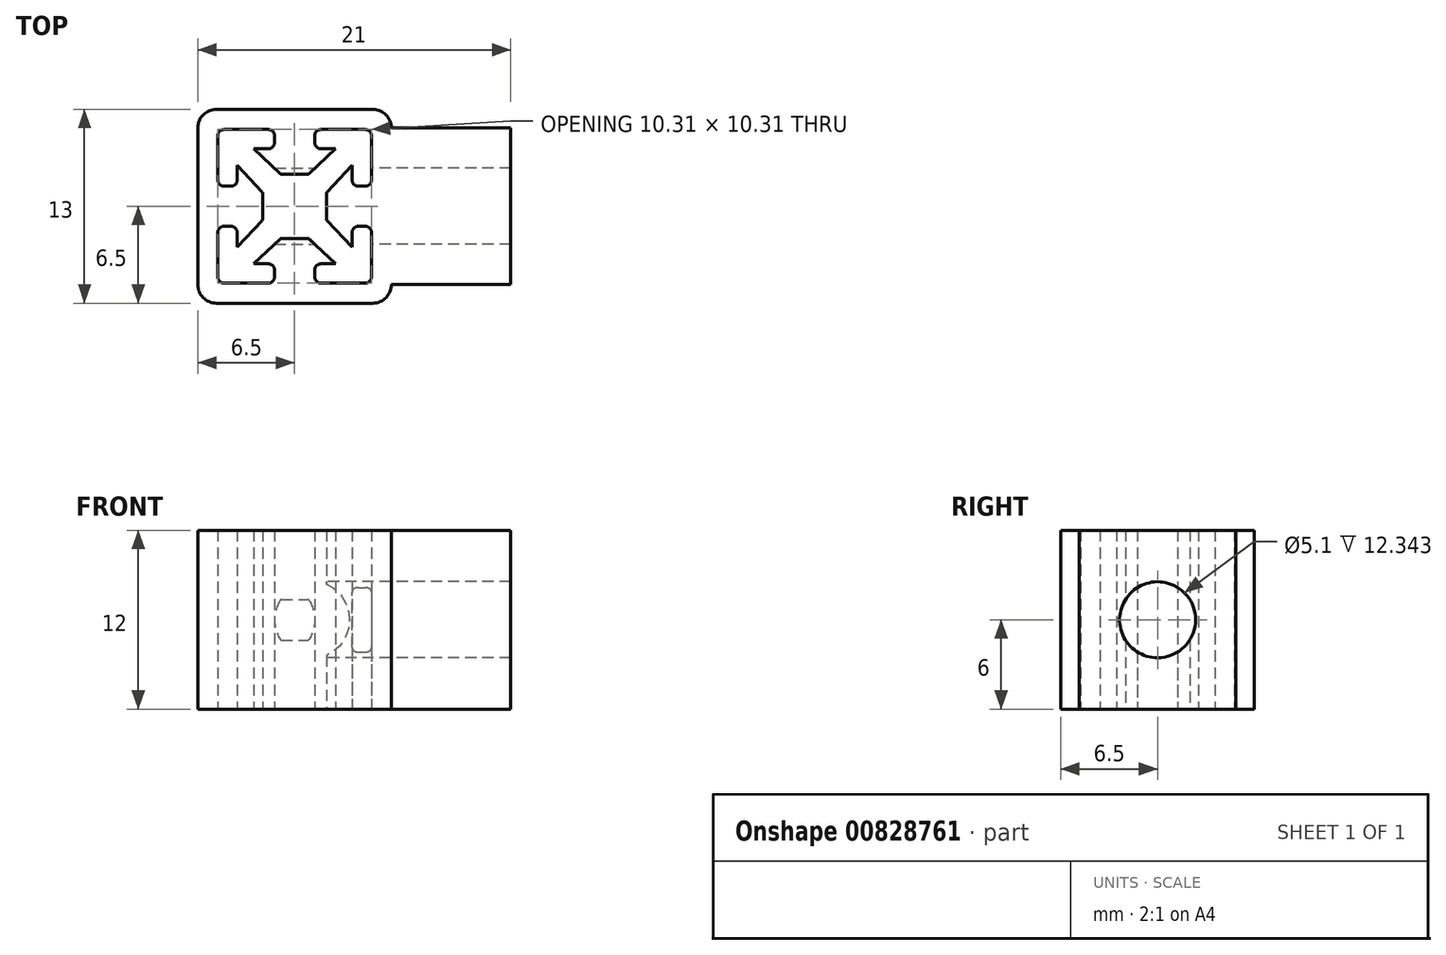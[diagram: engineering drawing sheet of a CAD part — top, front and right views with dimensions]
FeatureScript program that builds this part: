
annotation { "Feature Type Name" : "Feature", "Feature Type Description" : "" }
export const myFeature = defineFeature(function(context is Context, id is Id, definition is map)
    precondition{}
    {
        {
            var Q0;
            Q0=qCreatedBy(makeId("Top.planeOp"),FACE);
            var sketch = newSketch(context, id + "F0", { "sketchPlane" : qUnion([Q0])});
            skArc(sketch, "E0.0", {"start": v(6.5, 5.25) * mm, "mid": v(6.13, 6.13) * mm, "end": v(5.25, 6.5) * mm});
            skLineSegment(sketch, "E0.1", {"start": v(6.5, -5.25) * mm, "end": v(6.5, 5.25) * mm});
            skLineSegment(sketch, "E0.2", {"start": v(5.25, 6.5) * mm, "end": v(-5.25, 6.5) * mm});
            skArc(sketch, "E0.3", {"start": v(5.25, -6.5) * mm, "mid": v(6.13, -6.13) * mm, "end": v(6.5, -5.25) * mm});
            skArc(sketch, "E0.4", {"start": v(-5.25, 6.5) * mm, "mid": v(-6.13, 6.13) * mm, "end": v(-6.5, 5.25) * mm});
            skLineSegment(sketch, "E0.5", {"start": v(-6.5, 5.25) * mm, "end": v(-6.5, -5.25) * mm});
            skArc(sketch, "E0.6", {"start": v(-6.5, -5.25) * mm, "mid": v(-6.13, -6.13) * mm, "end": v(-5.25, -6.5) * mm});
            skLineSegment(sketch, "E0.7", {"start": v(-5.25, -6.5) * mm, "end": v(5.25, -6.5) * mm});
            skSolve(sketch);
        }
        {
            var Q0;
            Q0=qSketchRegion(id+"F0",true);
            extrude(context, id + "F1", {"entities" : qUnion([Q0]), "endBound" : BoundingType.SYMMETRIC, "oppositeDirection" : true, "depth" : 12 * mm, "offsetDistance" : 25 * mm});
        }
        {
            var Q0;
            Q0=qCreatedBy(makeId("Top.planeOp"),FACE);
            var sketch = newSketch(context, id + "F2", { "sketchPlane" : qUnion([Q0])});
            skLineSegment(sketch, "E1.0", {"start": v(0.96, -2.18) * mm, "end": v(2.75, -3.86) * mm});
            skArc(sketch, "E1.1", {"start": v(0.96, -2.18) * mm, "mid": v(0.93, -2.16) * mm, "end": v(0.89, -2.16) * mm});
            skLineSegment(sketch, "E1.2", {"start": v(0.89, -2.16) * mm, "end": v(-0.89, -2.16) * mm});
            skArc(sketch, "E1.3", {"start": v(-0.89, -2.16) * mm, "mid": v(-0.93, -2.16) * mm, "end": v(-0.96, -2.18) * mm});
            skLineSegment(sketch, "E1.4", {"start": v(-0.96, -2.18) * mm, "end": v(-2.75, -3.86) * mm});
            skLineSegment(sketch, "E1.5", {"start": v(-2.75, -3.86) * mm, "end": v(-1.75, -3.86) * mm});
            skArc(sketch, "E1.6", {"start": v(-1.35, -4.27) * mm, "mid": v(-1.47, -3.98) * mm, "end": v(-1.75, -3.86) * mm});
            skLineSegment(sketch, "E1.7", {"start": v(-1.35, -4.27) * mm, "end": v(-1.35, -4.75) * mm});
            skArc(sketch, "E1.8", {"start": v(-1.75, -5.15) * mm, "mid": v(-1.47, -5.04) * mm, "end": v(-1.35, -4.75) * mm});
            skLineSegment(sketch, "E1.9", {"start": v(-1.75, -5.15) * mm, "end": v(-4.75, -5.15) * mm});
            skArc(sketch, "E1.10", {"start": v(-5.15, -4.75) * mm, "mid": v(-5.04, -5.04) * mm, "end": v(-4.75, -5.15) * mm});
            skLineSegment(sketch, "E1.11", {"start": v(-5.15, -1.75) * mm, "end": v(-5.15, -4.75) * mm});
            skArc(sketch, "E1.12", {"start": v(-4.75, -1.35) * mm, "mid": v(-5.04, -1.47) * mm, "end": v(-5.15, -1.75) * mm});
            skLineSegment(sketch, "E1.13", {"start": v(-4.27, -1.35) * mm, "end": v(-4.75, -1.35) * mm});
            skArc(sketch, "E1.14", {"start": v(-3.86, -1.75) * mm, "mid": v(-3.98, -1.47) * mm, "end": v(-4.27, -1.35) * mm});
            skLineSegment(sketch, "E1.15", {"start": v(-3.86, -2.75) * mm, "end": v(-3.86, -1.75) * mm});
            skLineSegment(sketch, "E1.16", {"start": v(-2.18, -0.96) * mm, "end": v(-3.86, -2.75) * mm});
            skArc(sketch, "E1.17", {"start": v(-2.18, -0.96) * mm, "mid": v(-2.16, -0.93) * mm, "end": v(-2.16, -0.89) * mm});
            skArc(sketch, "E1.18", {"start": v(5.15, 4.75) * mm, "mid": v(5.04, 5.04) * mm, "end": v(4.75, 5.15) * mm});
            skLineSegment(sketch, "E1.19", {"start": v(5.15, 1.75) * mm, "end": v(5.15, 4.75) * mm});
            skArc(sketch, "E1.20", {"start": v(4.75, 1.35) * mm, "mid": v(5.04, 1.47) * mm, "end": v(5.15, 1.75) * mm});
            skLineSegment(sketch, "E1.21", {"start": v(4.27, 1.35) * mm, "end": v(4.75, 1.35) * mm});
            skArc(sketch, "E1.22", {"start": v(3.86, 1.75) * mm, "mid": v(3.98, 1.47) * mm, "end": v(4.27, 1.35) * mm});
            skLineSegment(sketch, "E1.23", {"start": v(3.86, 2.75) * mm, "end": v(3.86, 1.75) * mm});
            skLineSegment(sketch, "E1.24", {"start": v(2.18, 0.96) * mm, "end": v(3.86, 2.75) * mm});
            skArc(sketch, "E1.25", {"start": v(2.18, 0.96) * mm, "mid": v(2.16, 0.93) * mm, "end": v(2.16, 0.89) * mm});
            skLineSegment(sketch, "E1.26", {"start": v(2.16, 0.89) * mm, "end": v(2.16, -0.89) * mm});
            skArc(sketch, "E1.27", {"start": v(2.16, -0.89) * mm, "mid": v(2.16, -0.93) * mm, "end": v(2.18, -0.96) * mm});
            skLineSegment(sketch, "E1.28", {"start": v(2.18, -0.96) * mm, "end": v(3.86, -2.75) * mm});
            skLineSegment(sketch, "E1.29", {"start": v(3.86, -2.75) * mm, "end": v(3.86, -1.75) * mm});
            skArc(sketch, "E1.30", {"start": v(1.35, -4.75) * mm, "mid": v(1.47, -5.04) * mm, "end": v(1.75, -5.15) * mm});
            skLineSegment(sketch, "E1.31", {"start": v(1.35, -4.27) * mm, "end": v(1.35, -4.75) * mm});
            skArc(sketch, "E1.32", {"start": v(1.75, -3.86) * mm, "mid": v(1.47, -3.98) * mm, "end": v(1.35, -4.27) * mm});
            skLineSegment(sketch, "E1.33", {"start": v(2.75, -3.86) * mm, "end": v(1.75, -3.86) * mm});
            skLineSegment(sketch, "E1.34", {"start": v(1.75, -5.15) * mm, "end": v(4.75, -5.15) * mm});
            skArc(sketch, "E1.35", {"start": v(4.75, -5.15) * mm, "mid": v(5.04, -5.04) * mm, "end": v(5.15, -4.75) * mm});
            skLineSegment(sketch, "E1.36", {"start": v(5.15, -1.75) * mm, "end": v(5.15, -4.75) * mm});
            skArc(sketch, "E1.37", {"start": v(5.15, -1.75) * mm, "mid": v(5.04, -1.47) * mm, "end": v(4.75, -1.35) * mm});
            skLineSegment(sketch, "E1.38", {"start": v(4.27, -1.35) * mm, "end": v(4.75, -1.35) * mm});
            skArc(sketch, "E1.39", {"start": v(4.27, -1.35) * mm, "mid": v(3.98, -1.47) * mm, "end": v(3.86, -1.75) * mm});
            skLineSegment(sketch, "E1.40", {"start": v(1.75, 5.15) * mm, "end": v(4.75, 5.15) * mm});
            skArc(sketch, "E1.41", {"start": v(1.75, 5.15) * mm, "mid": v(1.47, 5.04) * mm, "end": v(1.35, 4.75) * mm});
            skLineSegment(sketch, "E1.42", {"start": v(1.35, 4.27) * mm, "end": v(1.35, 4.75) * mm});
            skArc(sketch, "E1.43", {"start": v(1.35, 4.27) * mm, "mid": v(1.47, 3.98) * mm, "end": v(1.75, 3.86) * mm});
            skLineSegment(sketch, "E1.44", {"start": v(2.75, 3.86) * mm, "end": v(1.75, 3.86) * mm});
            skLineSegment(sketch, "E1.45", {"start": v(0.96, 2.18) * mm, "end": v(2.75, 3.86) * mm});
            skArc(sketch, "E1.46", {"start": v(0.89, 2.16) * mm, "mid": v(0.93, 2.16) * mm, "end": v(0.96, 2.18) * mm});
            skLineSegment(sketch, "E1.47", {"start": v(-0.89, 2.16) * mm, "end": v(0.89, 2.16) * mm});
            skArc(sketch, "E1.48", {"start": v(-0.96, 2.18) * mm, "mid": v(-0.93, 2.16) * mm, "end": v(-0.89, 2.16) * mm});
            skLineSegment(sketch, "E1.49", {"start": v(-0.96, 2.18) * mm, "end": v(-2.75, 3.86) * mm});
            skLineSegment(sketch, "E1.50", {"start": v(-2.75, 3.86) * mm, "end": v(-1.75, 3.86) * mm});
            skArc(sketch, "E1.51", {"start": v(-1.75, 3.86) * mm, "mid": v(-1.47, 3.98) * mm, "end": v(-1.35, 4.27) * mm});
            skLineSegment(sketch, "E1.52", {"start": v(-1.35, 4.27) * mm, "end": v(-1.35, 4.75) * mm});
            skArc(sketch, "E1.53", {"start": v(-1.35, 4.75) * mm, "mid": v(-1.47, 5.04) * mm, "end": v(-1.75, 5.15) * mm});
            skLineSegment(sketch, "E1.54", {"start": v(-1.75, 5.15) * mm, "end": v(-4.75, 5.15) * mm});
            skArc(sketch, "E1.55", {"start": v(-4.75, 5.15) * mm, "mid": v(-5.04, 5.04) * mm, "end": v(-5.15, 4.75) * mm});
            skLineSegment(sketch, "E1.56", {"start": v(-5.15, 1.75) * mm, "end": v(-5.15, 4.75) * mm});
            skArc(sketch, "E1.57", {"start": v(-5.15, 1.75) * mm, "mid": v(-5.04, 1.47) * mm, "end": v(-4.75, 1.35) * mm});
            skLineSegment(sketch, "E1.58", {"start": v(-4.27, 1.35) * mm, "end": v(-4.75, 1.35) * mm});
            skArc(sketch, "E1.59", {"start": v(-4.27, 1.35) * mm, "mid": v(-3.98, 1.47) * mm, "end": v(-3.86, 1.75) * mm});
            skLineSegment(sketch, "E1.60", {"start": v(-3.86, 2.75) * mm, "end": v(-3.86, 1.75) * mm});
            skLineSegment(sketch, "E1.61", {"start": v(-2.18, 0.96) * mm, "end": v(-3.86, 2.75) * mm});
            skArc(sketch, "E1.62", {"start": v(-2.16, 0.89) * mm, "mid": v(-2.16, 0.93) * mm, "end": v(-2.18, 0.96) * mm});
            skLineSegment(sketch, "E1.63", {"start": v(-2.16, 0.89) * mm, "end": v(-2.16, -0.89) * mm});
            skSolve(sketch);
        }
        {
            var Q0;
            Q0=makeQuery(id+"F2.imprint","IMPRINT",FACE,{"disambiguationData":[TD([[makeQuery(id+"F2.imprint","IMPRINT",EDGE,{"derivedFrom":sQuery(id+"F2.wireOp",EDGE,"E1.0")}),1.0]])]});
            extrude(context, id + "F3", {"entities" : qUnion([Q0]), "operationType" : NewBodyOperationType.REMOVE, "endBound" : BoundingType.SYMMETRIC, "depth" : 20 * mm, "offsetDistance" : 25 * mm});
        }
        {
            var Q0;
            Q0=makeQuery(id+"F1.opExtrude","SWEPT_FACE",FACE,{"disambiguationData":[OSD([sQuery(id+"F0.wireOp",EDGE,"E0.1")])]});
            var sketch = newSketch(context, id + "F4", { "sketchPlane" : qUnion([Q0])});
            skCircle(sketch, "E2", {"center": v(0, 0) * mm, "radius": 2.55 * mm});
            skSolve(sketch);
        }
        {
            var Q0;
            Q0=makeQuery(id+"F4.imprint","IMPRINT",FACE,{"disambiguationData":[TD([[makeQuery(id+"F4.imprint","IMPRINT",EDGE,{"derivedFrom":sQuery(id+"F4.wireOp",EDGE,"E2")}),-1.0]])]});
            extrude(context, id + "F5", {"entities" : qUnion([Q0]), "operationType" : NewBodyOperationType.ADD, "depth" : 8 * mm, "offsetDistance" : 25 * mm});
        }
        {
            var Q0;
            Q0=makeQuery(id+"F1.opExtrude","SWEPT_FACE",FACE,{"disambiguationData":[OSD([sQuery(id+"F0.wireOp",EDGE,"E0.1")])]});
            var Q1;
            Q1=makeQuery(id+"F3.boolean.opBoolean","COPY",FACE,{"derivedFrom":makeQuery(id+"F3.opExtrude","SWEPT_FACE",FACE,{"disambiguationData":[OSD([sQuery(id+"F2.wireOp",EDGE,"E1.63")])]})});
            extrude(context, id + "F6", {"entities" : qUnion([Q0]), "operationType" : NewBodyOperationType.REMOVE, "endBound" : BoundingType.UP_TO_SURFACE, "oppositeDirection" : true, "depth" : 25 * mm, "endBoundEntityFace" : qUnion([Q1]), "offsetDistance" : 25 * mm});
        }
    });
